FCSTD DOCUMENT  (FreeCAD 0.21R33771 (Git))
Label: fodo
License: All rights reserved
LicenseURL: https://en.wikipedia.org/wiki/All_rights_reserved
objects: Sketcher::SketchObject×1, PartDesign::Body×1
note: 2 computed .brp shape members not serialized (recipe doc carries the construction recipe); baked Part::Feature solids carry a one-line shape summary decoded from their .brp

FEATURE [Sketcher::SketchObject] Sketch
  FullyConstrained = false
  MapMode = 2
  sketch-geometry (96):
    g0: LineSegment StartX=-55.585 StartY=21 StartZ=0 EndX=-43.585 EndY=21 EndZ=0
    g1: LineSegment StartX=-55.585 StartY=-21 StartZ=0 EndX=-43.585 EndY=-21 EndZ=0
    g2: LineSegment StartX=-55.585 StartY=21 StartZ=0 EndX=-55.585 EndY=-21 EndZ=0
    g3: LineSegment StartX=-43.585 StartY=-21 StartZ=0 EndX=-43.585 EndY=21 EndZ=0
    g4: ArcOfCircle CenterX=-120.261 CenterY=0 CenterZ=0 NormalX=0 NormalY=0 NormalZ=1 AngleXU=0 Radius=68 StartAngle=5.96923 EndAngle=6.59714
    g5: ArcOfCircle CenterX=21.0911 CenterY=7.90527e-07 CenterZ=0 NormalX=0 NormalY=0 NormalZ=1 AngleXU=0 Radius=68 StartAngle=2.82764 EndAngle=3.45555
    g6: LineSegment StartX=-1.58504 StartY=21 StartZ=0 EndX=10.415 EndY=21 EndZ=0
    g7: LineSegment StartX=-1.58504 StartY=-21 StartZ=0 EndX=10.415 EndY=-21 EndZ=0
    g8: LineSegment StartX=-1.58504 StartY=21 StartZ=0 EndX=-1.58504 EndY=-21 EndZ=0
    g9: LineSegment StartX=10.415 StartY=-21 StartZ=0 EndX=10.415 EndY=21 EndZ=0
    g10: ArcOfCircle CenterX=-66.2612 CenterY=1.3e-15 CenterZ=0 NormalX=0 NormalY=0 NormalZ=1 AngleXU=0 Radius=68 StartAngle=5.96923 EndAngle=6.59714
    g11: ArcOfCircle CenterX=75.0911 CenterY=-2.93312e-07 CenterZ=0 NormalX=0 NormalY=0 NormalZ=1 AngleXU=0 Radius=68 StartAngle=2.82764 EndAngle=3.45555
    g12: LineSegment StartX=-43.585 StartY=-21 StartZ=0 EndX=-1.58504 EndY=-21 EndZ=0
    g13: LineSegment StartX=52.415 StartY=21 StartZ=0 EndX=64.415 EndY=21 EndZ=0
    g14: LineSegment StartX=52.415 StartY=-21 StartZ=0 EndX=64.415 EndY=-21 EndZ=0
    g15: LineSegment StartX=52.415 StartY=21 StartZ=0 EndX=52.415 EndY=-21 EndZ=0
    g16: LineSegment StartX=64.415 StartY=-21 StartZ=0 EndX=64.415 EndY=21 EndZ=0
    g17: ArcOfCircle CenterX=-12.2612 CenterY=-1e-15 CenterZ=0 NormalX=0 NormalY=0 NormalZ=1 AngleXU=0 Radius=68 StartAngle=5.96923 EndAngle=6.59714
    g18: ArcOfCircle CenterX=129.091 CenterY=4.66298e-07 CenterZ=0 NormalX=0 NormalY=0 NormalZ=1 AngleXU=0 Radius=68 StartAngle=2.82764 EndAngle=3.45555
    g19: LineSegment StartX=10.415 StartY=-21 StartZ=0 EndX=52.415 EndY=-21 EndZ=0
    g20: LineSegment StartX=-43.585 StartY=21 StartZ=0 EndX=-1.58504 EndY=21 EndZ=0
    g21: LineSegment StartX=10.415 StartY=21 StartZ=0 EndX=52.415 EndY=21 EndZ=0
    g22: LineSegment StartX=-23.585 StartY=21 StartZ=0 EndX=-21.585 EndY=21 EndZ=0
    g23: LineSegment StartX=-23.585 StartY=-21 StartZ=0 EndX=-21.585 EndY=-21 EndZ=0
    g24: ArcOfCircle CenterX=41.0911 CenterY=0 CenterZ=0 NormalX=0 NormalY=0 NormalZ=1 AngleXU=0 Radius=68 StartAngle=2.82764 EndAngle=3.45555
    g25: ArcOfCircle CenterX=-86.2612 CenterY=0 CenterZ=0 NormalX=0 NormalY=0 NormalZ=1 AngleXU=0 Radius=68 StartAngle=5.96923 EndAngle=6.59714
    g26: LineSegment StartX=-43.585 StartY=21 StartZ=0 EndX=-23.585 EndY=21 EndZ=0
    g27: LineSegment StartX=-21.585 StartY=21 StartZ=0 EndX=-1.58504 EndY=21 EndZ=0
    g28: ArcOfCircle CenterX=95.0911 CenterY=0 CenterZ=0 NormalX=0 NormalY=0 NormalZ=1 AngleXU=0 Radius=68 StartAngle=2.82764 EndAngle=3.45555
    g29: ArcOfCircle CenterX=-32.2612 CenterY=0 CenterZ=0 NormalX=0 NormalY=0 NormalZ=1 AngleXU=0 Radius=68 StartAngle=5.96923 EndAngle=6.59714
    g30: LineSegment StartX=30.415 StartY=21 StartZ=0 EndX=32.415 EndY=21 EndZ=0
    g31: LineSegment StartX=30.415 StartY=-21 StartZ=0 EndX=32.415 EndY=-21 EndZ=0
    g32: LineSegment StartX=10.415 StartY=21 StartZ=0 EndX=30.415 EndY=21 EndZ=0
    g33: LineSegment StartX=32.415 StartY=21 StartZ=0 EndX=52.415 EndY=21 EndZ=0
    g34: LineSegment StartX=-65.585 StartY=0 StartZ=0 EndX=74.415 EndY=0 EndZ=0
    g35: LineSegment StartX=-65.585 StartY=0 StartZ=0 EndX=-55.585 EndY=21 EndZ=0
    g36: LineSegment StartX=74.415 StartY=0 StartZ=0 EndX=64.415 EndY=-21 EndZ=0
    g37: LineSegment StartX=-65.585 StartY=0 StartZ=0 EndX=-55.585 EndY=0 EndZ=0
    g38: LineSegment StartX=-65.585 StartY=-16 StartZ=0 EndX=-49.585 EndY=-4.31 EndZ=0
    g39: LineSegment StartX=-49.585 StartY=-4.31 StartZ=0 EndX=-22.585 EndY=0 EndZ=0
    g40: LineSegment StartX=-22.585 StartY=0 StartZ=0 EndX=4.41496 EndY=4.31 EndZ=0
    g41: LineSegment StartX=4.41496 StartY=4.31 StartZ=0 EndX=31.415 EndY=16 EndZ=0
    g42: LineSegment StartX=31.415 StartY=16 StartZ=0 EndX=58.415 EndY=4.29041 EndZ=0
    g43: LineSegment StartX=58.415 StartY=4.29041 StartZ=0 EndX=74.415 EndY=3.11771 EndZ=0
    g44: LineSegment StartX=4.41496 StartY=4.31 StartZ=0 EndX=4.41496 EndY=0 EndZ=0
    g45: LineSegment StartX=58.415 StartY=4.29041 StartZ=0 EndX=58.8255 EndY=0 EndZ=0
    g46: LineSegment StartX=74.415 StartY=0 StartZ=0 EndX=74.415 EndY=3.11771 EndZ=0
    g47: LineSegment StartX=-49.585 StartY=-4.31 StartZ=0 EndX=-49.585 EndY=0 EndZ=0
    g48: LineSegment StartX=-52.2612 StartY=0 StartZ=0 EndX=-49.585 EndY=0 EndZ=0
    g49: LineSegment StartX=-49.585 StartY=0 StartZ=0 EndX=-46.9089 EndY=0 EndZ=0
    g50: LineSegment StartX=-65.585 StartY=0 StartZ=0 EndX=-65.585 EndY=-16 EndZ=0
    g51: LineSegment StartX=-22.585 StartY=0 StartZ=0 EndX=-26.9089 EndY=0 EndZ=0
    g52: LineSegment StartX=-22.585 StartY=0 StartZ=0 EndX=-18.2612 EndY=0 EndZ=0
    g53: LineSegment StartX=4.41496 StartY=0 StartZ=0 EndX=1.73885 EndY=0 EndZ=0
    g54: LineSegment StartX=4.41496 StartY=0 StartZ=0 EndX=7.09108 EndY=0 EndZ=0
    g55: LineSegment StartX=31.415 StartY=16 StartZ=0 EndX=29.0002 EndY=16 EndZ=0
    g56: LineSegment StartX=31.415 StartY=16 StartZ=0 EndX=33.8297 EndY=16 EndZ=0
    g57: LineSegment StartX=58.415 StartY=4.29041 StartZ=0 EndX=55.6034 EndY=4.29041 EndZ=0
    g58: LineSegment StartX=58.415 StartY=4.29041 StartZ=0 EndX=61.2266 EndY=4.29041 EndZ=0
    g59: LineSegment StartX=31.415 StartY=17.403 StartZ=0 EndX=4.41496 EndY=5.71299 EndZ=0
    g60: LineSegment StartX=4.41496 StartY=5.71299 StartZ=0 EndX=-22.585 EndY=17.403 EndZ=0
    g61: LineSegment StartX=-22.585 StartY=17.403 StartZ=0 EndX=-49.585 EndY=5.71299 EndZ=0
    g62: LineSegment StartX=-49.585 StartY=5.71299 StartZ=0 EndX=-65.585 EndY=17.403 EndZ=0
    g63: LineSegment StartX=31.415 StartY=17.403 StartZ=0 EndX=58.415 EndY=5.71299 EndZ=0
    g64: LineSegment StartX=58.415 StartY=5.71299 StartZ=0 EndX=74.852 EndY=17.403 EndZ=0
    g65: LineSegment StartX=31.415 StartY=16 StartZ=0 EndX=31.415 EndY=17.403 EndZ=0
    g66: LineSegment StartX=4.41496 StartY=5.71299 StartZ=0 EndX=4.41496 EndY=4.31 EndZ=0
    g67: LineSegment StartX=31.415 StartY=16 StartZ=0 EndX=31.415 EndY=0 EndZ=0
    g68: LineSegment StartX=58.415 StartY=4.29041 StartZ=0 EndX=58.415 EndY=5.71299 EndZ=0
    g69: LineSegment StartX=-22.585 StartY=17.403 StartZ=0 EndX=31.415 EndY=17.403 EndZ=0
    g70: LineSegment StartX=-22.585 StartY=17.403 StartZ=0 EndX=-22.585 EndY=0 EndZ=0
    g71: LineSegment StartX=-49.585 StartY=0 StartZ=0 EndX=-49.585 EndY=5.71299 EndZ=0
    g72: LineSegment StartX=4.41496 StartY=5.71299 StartZ=0 EndX=-49.585 EndY=5.71299 EndZ=0
    g73: LineSegment StartX=4.41496 StartY=5.71299 StartZ=0 EndX=58.415 EndY=5.71299 EndZ=0
    g74: LineSegment StartX=31.415 StartY=17.403 StartZ=0 EndX=74.852 EndY=17.403 EndZ=0
    g75: LineSegment StartX=-65.585 StartY=17.403 StartZ=0 EndX=-22.585 EndY=17.403 EndZ=0
    g76: LineSegment StartX=-65.585 StartY=0 StartZ=0 EndX=-65.585 EndY=17.403 EndZ=0
    g77: LineSegment StartX=74.415 StartY=3.11771 StartZ=0 EndX=74.852 EndY=17.403 EndZ=0
    g78: LineSegment StartX=-65.585 StartY=-17.403 StartZ=0 EndX=-49.585 EndY=-5.71299 EndZ=0
    g79: LineSegment StartX=-49.585 StartY=-5.71299 StartZ=0 EndX=-22.585 EndY=-17.403 EndZ=0
    g80: LineSegment StartX=-22.585 StartY=-17.403 StartZ=0 EndX=4.41496 EndY=-5.71299 EndZ=0
    g81: LineSegment StartX=4.41496 StartY=-5.71299 StartZ=0 EndX=31.415 EndY=-17.403 EndZ=0
    g82: LineSegment StartX=31.415 StartY=-17.403 StartZ=0 EndX=58.8255 EndY=-5.72771 EndZ=0
    g83: LineSegment StartX=58.8255 StartY=-5.72771 StartZ=0 EndX=74.415 EndY=-17.4085 EndZ=0
    g84: LineSegment StartX=74.415 StartY=-17.4085 StartZ=0 EndX=74.415 EndY=0 EndZ=0
    g85: LineSegment StartX=58.8255 StartY=-5.72771 StartZ=0 EndX=58.8255 EndY=0 EndZ=0
    g86: LineSegment StartX=31.415 StartY=-17.403 StartZ=0 EndX=31.415 EndY=0 EndZ=0
    g87: LineSegment StartX=4.41496 StartY=-5.71299 StartZ=0 EndX=4.41496 EndY=0 EndZ=0
    g88: LineSegment StartX=-22.585 StartY=-17.403 StartZ=0 EndX=-22.585 EndY=0 EndZ=0
    g89: LineSegment StartX=-65.585 StartY=-17.403 StartZ=0 EndX=-65.585 EndY=0 EndZ=0
    g90: LineSegment StartX=-49.585 StartY=0 StartZ=0 EndX=-49.585 EndY=-5.71299 EndZ=0
    g91: LineSegment StartX=4.41496 StartY=5.71299 StartZ=0 EndX=4.88032 EndY=0 EndZ=0
    g92: LineSegment StartX=4.41496 StartY=5.71299 StartZ=0 EndX=4.41496 EndY=0 EndZ=0
    g93: LineSegment StartX=31.415 StartY=17.403 StartZ=0 EndX=31.415 EndY=0 EndZ=0
    g94: LineSegment StartX=58.415 StartY=5.71299 StartZ=0 EndX=58.8255 EndY=0 EndZ=0
    g95: LineSegment StartX=74.415 StartY=0 StartZ=0 EndX=74.852 EndY=17.403 EndZ=0
  constraints (254):
    c: Horizontal(g0)
    c: Horizontal(g1)
    c: Coincident(g2,g0)
    c: Coincident(g2,g1)
    c: Coincident(g3,g1)
    c: Coincident(g3,g0)
    c: Equal(g3,g2)
    c: Angle(g1,g2) = 1.5708
    c: Coincident(g4,g0)
    c: Coincident(g4,g1)
    c: Coincident(g5,g0)
    c: Coincident(g5,g1)
    c: Equal(g5,g4)
    c: Horizontal(g6)
    c: Horizontal(g7)
    c: Coincident(g8,g6)
    c: Coincident(g8,g7)
    c: Coincident(g9,g7)
    c: Coincident(g9,g6)
    c: Equal(g9,g8)
    c: Angle(g7,g8) = 1.5708
    c: Coincident(g10,g6)
    c: Coincident(g10,g7)
    c: Coincident(g11,g6)
    c: Coincident(g11,g7)
    c: Equal(g11,g10)
    c: Coincident(g12,g1)
    c: Coincident(g12,g7)
    c: Parallel(g0,g12)
    c: Equal(g8,g3)
    c: Equal(g6,g0)
    c: DistanceX(g0,g0) = 12
    c: Equal(g10,g4)
    c: Radius(g4) = 68
    c: DistanceY(g9,g9) = 42
    c: Horizontal(g13)
    c: Horizontal(g14)
    c: Coincident(g15,g13)
    c: Coincident(g15,g14)
    c: Coincident(g16,g14)
    c: Coincident(g16,g13)
    c: Equal(g16,g15)
    c: Angle(g14,g15) = 1.5708
    c: Coincident(g17,g13)
    c: Coincident(g17,g14)
    c: Coincident(g18,g13)
    c: Coincident(g18,g14)
    c: Equal(g18,g17)
    c: Coincident(g19,g14)
    c: Equal(g9,g16) = 42
    c: Coincident(g7,g19)
    c: Parallel(g12,g19)
    c: Equal(g11,g18)
    c: Equal(g6,g13)
    c: Equal(g19,g12)
    c: Coincident(g20,g0)
    c: Coincident(g20,g6)
    c: Coincident(g21,g6)
    c: Coincident(g21,g13)
    c: PointOnObject(g22,g20)
    c: PointOnObject(g22,g20)
    c: PointOnObject(g23,g12)
    c: PointOnObject(g23,g12)
    c: Coincident(g24,g22)
    c: Coincident(g24,g23)
    c: Equal(g4,g24)
    c: Coincident(g25,g22)
    c: Coincident(g25,g23)
    c: Equal(g24,g25)
    c: PointOnObject(g24,g-1)
    c: PointOnObject(g4,g-1)
    c: PointOnObject(g25,g-1)
    c: DistanceX(g22,g22) = 2
    c: Coincident(g26,g0)
    c: Coincident(g26,g22)
    c: Coincident(g27,g22)
    c: Coincident(g27,g6)
    c: Equal(g26,g27)
    c: Coincident(g28,g30)
    c: Coincident(g28,g31)
    c: Coincident(g29,g30)
    c: Coincident(g29,g31)
    c: Equal(g28,g29)
    c: Equal(g22,g30) = 2
    c: PointOnObject(g28,g21)
    c: PointOnObject(g29,g21)
    c: PointOnObject(g28,g19)
    c: PointOnObject(g29,g19)
    c: Equal(g25,g29)
    c: PointOnObject(g28,g-1)
    c: PointOnObject(g29,g-1)
    c: Coincident(g32,g6)
    c: Coincident(g32,g28)
    c: Coincident(g33,g29)
    c: Coincident(g33,g13)
    c: Equal(g32,g33)
    c: PointOnObject(g34,g-1)
    c: PointOnObject(g34,g-1)
    c: Coincident(g35,g34)
    c: Coincident(g35,g0)
    c: Coincident(g36,g34)
    c: Coincident(g36,g14)
    c: Equal(g36,g35)
    c: Coincident(g37,g34)
    c: PointOnObject(g37,g34)
    c: DistanceX(g37,g37) = 10
    c: PointOnObject(g37,g2)
    c: Coincident(g38,g39)
    c: PointOnObject(g39,g34)
    c: Coincident(g39,g40)
    c: Coincident(g40,g41)
    c: Coincident(g41,g42)
    c: Coincident(g42,g43)
    c: Coincident(g44,g40)
    c: PointOnObject(g44,g34)
    c: Vertical(g44)
    c: Coincident(g45,g42)
    c: PointOnObject(g45,g34)
    c: Equal(g45,g44)
    c: Coincident(g46,g34)
    c: Coincident(g46,g43)
    c: Vertical(g46)
    c: Coincident(g47,g38)
    c: PointOnObject(g47,g34)
    c: Vertical(g47)
    c: Equal(g44,g47)
    c: PointOnObject(g48,g4)
    c: Coincident(g48,g47)
    c: Horizontal(g48)
    c: Coincident(g49,g47)
    c: PointOnObject(g49,g5)
    c: Horizontal(g49)
    c: Equal(g48,g49)
    c: Coincident(g50,g34)
    c: Coincident(g50,g38)
    c: Vertical(g50)
    c: DistanceX(g20,g20) = 42
    c: Coincident(g51,g39)
    c: PointOnObject(g51,g24)
    c: Horizontal(g51)
    c: Coincident(g52,g39)
    c: PointOnObject(g52,g25)
    c: Horizontal(g52)
    c: Equal(g51,g52)
    c: Coincident(g53,g44)
    c: PointOnObject(g53,g10)
    c: Horizontal(g53)
    c: Coincident(g54,g44)
    c: PointOnObject(g54,g11)
    c: Horizontal(g54)
    c: Equal(g53,g54)
    c: Coincident(g55,g41)
    c: PointOnObject(g55,g28)
    c: Horizontal(g55)
    c: Coincident(g56,g41)
    c: PointOnObject(g56,g29)
    c: Horizontal(g56)
    c: Equal(g56,g55)
    c: Coincident(g57,g42)
    c: PointOnObject(g57,g17)
    c: Horizontal(g57)
    c: Coincident(g58,g42)
    c: PointOnObject(g58,g18)
    c: Horizontal(g58)
    c: Equal(g58,g57)
    c: Coincident(g60,g59)
    c: Coincident(g61,g60)
    c: Coincident(g62,g61)
    c: Coincident(g63,g59)
    c: Coincident(g64,g63)
    c: Coincident(g65,g41)
    c: Coincident(g65,g59)
    c: Vertical(g65)
    c: Coincident(g66,g59)
    c: Coincident(g66,g40)
    c: Vertical(g66)
    c: Equal(g65,g66)
    c: DistanceY(g47,g47) = 4.31
    c: DistanceY(g50,g50) = 16
    c: Coincident(g67,g41)
    c: PointOnObject(g67,g34)
    c: Vertical(g67)
    c: DistanceY(g67,g67) = 16
    c: Coincident(g68,g42)
    c: Coincident(g68,g63)
    c: Vertical(g68)
    c: Coincident(g69,g60)
    c: Coincident(g69,g59)
    c: Horizontal(g69)
    c: Coincident(g70,g60)
    c: Coincident(g70,g39)
    c: Vertical(g70)
    c: Coincident(g71,g47)
    c: Coincident(g71,g61)
    c: Vertical(g71)
    c: Coincident(g72,g59)
    c: Coincident(g72,g61)
    c: Horizontal(g72)
    c: Coincident(g73,g59)
    c: Coincident(g73,g63)
    c: Horizontal(g73)
    c: Coincident(g74,g59)
    c: Coincident(g74,g64)
    c: Horizontal(g74)
    c: Coincident(g75,g62)
    c: Coincident(g75,g60)
    c: Horizontal(g75)
    c: Coincident(g76,g34)
    c: Coincident(g76,g62)
    c: Vertical(g76)
    c: Coincident(g77,g43)
    c: Coincident(g77,g64)
    c: Coincident(g78,g79)
    c: Coincident(g79,g80)
    c: Coincident(g80,g81)
    c: Coincident(g81,g82)
    c: Coincident(g82,g83)
    c: Coincident(g84,g83)
    c: Coincident(g84,g34)
    c: Vertical(g84)
    c: Coincident(g85,g82)
    c: Coincident(g85,g45)
    c: Coincident(g86,g81)
    c: Coincident(g86,g67)
    c: Vertical(g86)
    c: Vertical(g85)
    c: Coincident(g87,g80)
    c: Coincident(g87,g44)
    c: Vertical(g87)
    c: Coincident(g88,g79)
    c: Coincident(g88,g39)
    c: Vertical(g88)
    c: Coincident(g89,g78)
    c: Coincident(g89,g34)
    c: Vertical(g89)
    c: Equal(g89,g76)
    c: Coincident(g90,g47)
    c: Coincident(g90,g78)
    c: Vertical(g90)
    c: Equal(g71,g90)
    c: Equal(g88,g70)
    c: Coincident(g91,g59)
    c: Coincident(g92,g59)
    c: Coincident(g92,g44)
    c: Equal(g92,g87)
    c: Coincident(g93,g59)
    c: Coincident(g93,g67)
    c: Equal(g93,g86)
    c: Coincident(g94,g63)
    c: Coincident(g94,g45)
    c: Equal(g94,g85)
    c: Coincident(g95,g34)
    c: Coincident(g95,g64)
    c: Equal(g95,g84)
FEATURE [PartDesign::Body] Body
  Group = -> [Sketch]
  Origin = -> Origin001
